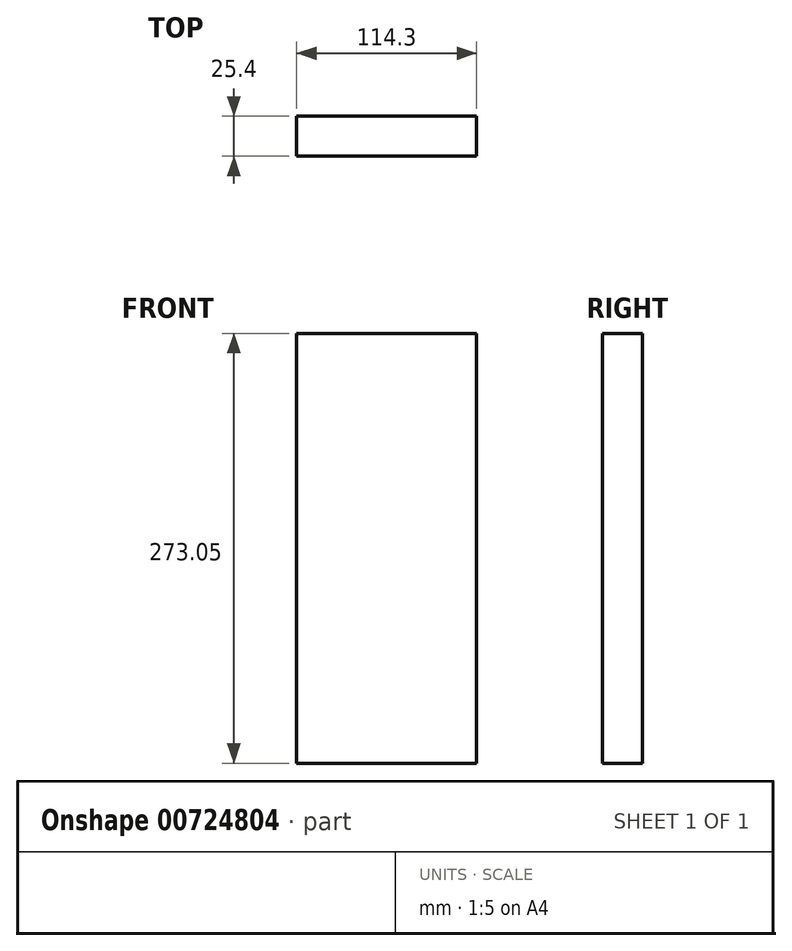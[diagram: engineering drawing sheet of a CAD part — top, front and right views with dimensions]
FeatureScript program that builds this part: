
annotation { "Feature Type Name" : "Feature", "Feature Type Description" : "" }
export const myFeature = defineFeature(function(context is Context, id is Id, definition is map)
    precondition{}
    {
        {
            var Q0;
            Q0=qCreatedBy(makeId("Front.planeOp"),FACE);
            var sketch = newSketch(context, id + "F0", { "sketchPlane" : qUnion([Q0])});
            skLineSegment(sketch, "E0.bottom", {"start": v(0, 0) * mm, "end": v(114.3, 0) * mm});
            skLineSegment(sketch, "E0.top", {"start": v(0, 273.05) * mm, "end": v(114.3, 273.05) * mm});
            skLineSegment(sketch, "E0.left", {"start": v(0, 0) * mm, "end": v(0, 273.05) * mm});
            skLineSegment(sketch, "E0.right", {"start": v(114.3, 0) * mm, "end": v(114.3, 273.05) * mm});
            skSolve(sketch);
        }
        {
            var Q0;
            Q0=makeQuery(id+"F0.imprint","IMPRINT",FACE,{"disambiguationData":[TD([[makeQuery(id+"F0.imprint","IMPRINT",EDGE,{"derivedFrom":sQuery(id+"F0.wireOp",EDGE,"E0.bottom")}),1.0]])]});
            extrude(context, id + "F1", {"entities" : qUnion([Q0]), "depth" : 25.4 * mm, "offsetDistance" : 25.4 * mm});
        }
    });
